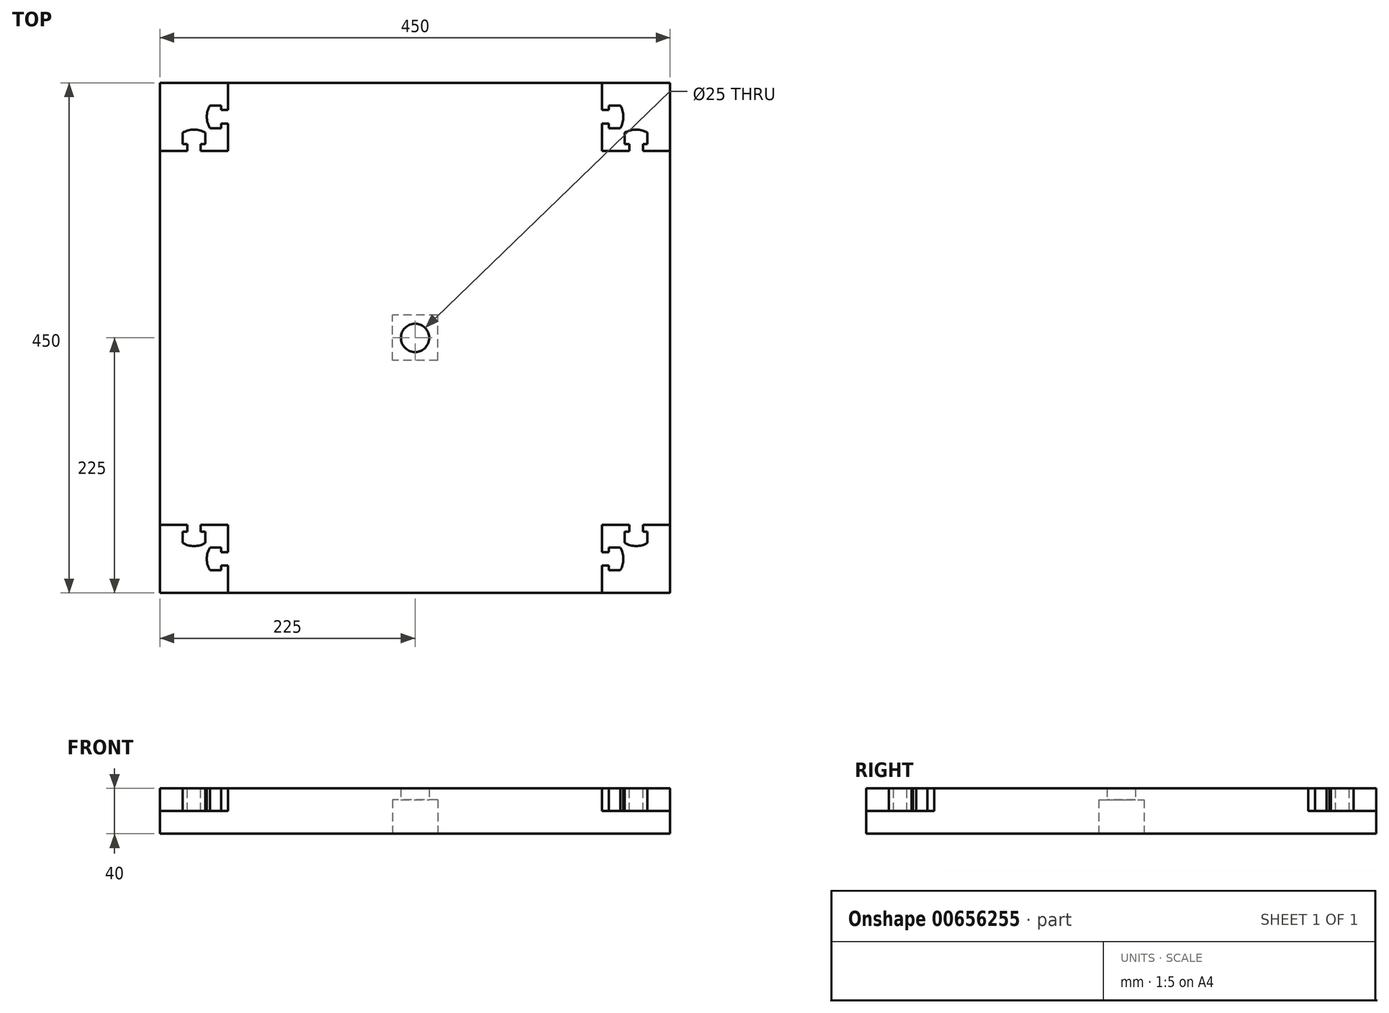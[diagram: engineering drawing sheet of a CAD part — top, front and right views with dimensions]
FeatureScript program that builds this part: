
annotation { "Feature Type Name" : "Feature", "Feature Type Description" : "" }
export const myFeature = defineFeature(function(context is Context, id is Id, definition is map)
    precondition{}
    {
        {
            var Q0;
            Q0=qCreatedBy(makeId("Top.planeOp"),FACE);
            var sketch = newSketch(context, id + "F0", { "sketchPlane" : qUnion([Q0])});
            skLineSegment(sketch, "E0.bottom", {"start": v(225, 225) * mm, "end": v(-225, 225) * mm});
            skLineSegment(sketch, "E0.top", {"start": v(225, -225) * mm, "end": v(-225, -225) * mm});
            skLineSegment(sketch, "E0.left", {"start": v(225, 225) * mm, "end": v(225, -225) * mm});
            skLineSegment(sketch, "E0.right", {"start": v(-225, 225) * mm, "end": v(-225, -225) * mm});
            skPoint(sketch, "E0.middle", {"position": v(0, 0) * mm});
            skLineSegment(sketch, "E1", {"start": v(-225, 165) * mm, "end": v(-165, 165) * mm});
            skLineSegment(sketch, "E2", {"start": v(-165, 165) * mm, "end": v(-165, 225) * mm});
            skLineSegment(sketch, "E3.MirrorCS", {"start": v(-225, -165) * mm, "end": v(-165, -165) * mm});
            skLineSegment(sketch, "E4.MirrorCS", {"start": v(-165, -165) * mm, "end": v(-165, -225) * mm});
            skLineSegment(sketch, "E5.MirrorCS", {"start": v(165, 165) * mm, "end": v(165, 225) * mm});
            skLineSegment(sketch, "E6.MirrorCS", {"start": v(225, 165) * mm, "end": v(165, 165) * mm});
            skLineSegment(sketch, "E7.MirrorCS", {"start": v(225, -165) * mm, "end": v(165, -165) * mm});
            skLineSegment(sketch, "E8.MirrorCS", {"start": v(165, -165) * mm, "end": v(165, -225) * mm});
            skSolve(sketch);
        }
        {
            var Q0;
            {var subQ4=sQuery(id+"F0.wireOp",EDGE,"E1");Q0=makeQuery(id+"F0.imprint","IMPRINT",FACE,{"disambiguationData":[TD([[makeQuery(id+"F0.imprint","IMPRINT",EDGE,{"derivedFrom":subQ4}),-1.0]])]});}
            extrude(context, id + "F1", {"entities" : qUnion([Q0]), "depth" : 40 * mm, "offsetDistance" : 25 * mm});
        }
        {
            var Q0;
            Q0=makeQuery(id+"FjshT1yFeJQ6c4P_1.boolean.opBoolean","MERGE",FACE,{"derivedFrom":[makeQuery(id+"F1.opExtrude","CAP_FACE",FACE,{"disambiguationData":[OSD([sQuery(id+"F0.wireOp",EDGE,"E0.bottom"),sQuery(id+"F0.wireOp",EDGE,"E0.top"),sQuery(id+"F0.wireOp",EDGE,"E0.left"),sQuery(id+"F0.wireOp",EDGE,"E0.right"),sQuery(id+"F0.wireOp",EDGE,"E1"),sQuery(id+"F0.wireOp",EDGE,"E2"),sQuery(id+"F0.wireOp",EDGE,"E3.MirrorCS"),sQuery(id+"F0.wireOp",EDGE,"E4.MirrorCS"),sQuery(id+"F0.wireOp",EDGE,"E5.MirrorCS"),sQuery(id+"F0.wireOp",EDGE,"E6.MirrorCS"),sQuery(id+"F0.wireOp",EDGE,"E7.MirrorCS"),sQuery(id+"F0.wireOp",EDGE,"E8.MirrorCS")])],"isStart":false}),makeQuery(id+"FjshT1yFeJQ6c4P_1.opExtrude","CAP_FACE",FACE,{"disambiguationData":[OSD([sQuery(id+"FFJnwm880kq7QGe_1.wireOp",EDGE,"IpZQhXBL-CYih-avNn-Q1HJ-p8kexNwLDa1K"),sQuery(id+"FFJnwm880kq7QGe_1.wireOp",EDGE,"DlTROYIy-GDss-TSJb-fTrS-hMDKvWpxQDZU"),sQuery(id+"FFJnwm880kq7QGe_1.wireOp",EDGE,"bTENbA7q-pvXI-0GNu-Zogf-TinsMhO668xT"),sQuery(id+"FFJnwm880kq7QGe_1.wireOp",EDGE,"CV59ftxt-n5LR-UtjV-LxEI-1yjvkEDBIUn7"),sQuery(id+"FFJnwm880kq7QGe_1.wireOp",EDGE,"VoNmPI9z-NIw1-XeOp-dFSM-tXPidPHyete0"),sQuery(id+"FFJnwm880kq7QGe_1.wireOp",EDGE,"zehCizCF-2Cgd-Ufk7-S7Fe-3zTjVviyliAL"),sQuery(id+"FFJnwm880kq7QGe_1.wireOp",EDGE,"YVxsESHW-nWeJ-Wa03-N7XI-iGOGesEvdSq9"),sQuery(id+"FFJnwm880kq7QGe_1.wireOp",EDGE,"igbJnYST-q3vv-sdNJ-N0c4-YNNVs6zLT43V")])],"isStart":true}),makeQuery(id+"FjshT1yFeJQ6c4P_1.opExtrude","CAP_FACE",FACE,{"disambiguationData":[OSD([sQuery(id+"FFJnwm880kq7QGe_1.wireOp",EDGE,"N9AVfqYu-QtxK-6Ad7-DoZk-YeEwseCOC2Zx"),sQuery(id+"FFJnwm880kq7QGe_1.wireOp",EDGE,"2Zl7s7qh-2swf-lT0q-C8q8-jJXlbCIyUqga"),sQuery(id+"FFJnwm880kq7QGe_1.wireOp",EDGE,"SRCtbRJ9-xsi2-BQLM-Kzfs-NWcCmin3xKqc"),sQuery(id+"FFJnwm880kq7QGe_1.wireOp",EDGE,"xzpgzOg8-CJKq-86Ur-ihYN-3kbHdTykDBMx"),sQuery(id+"FFJnwm880kq7QGe_1.wireOp",EDGE,"zk2CsXnC-Ixh2-XMb2-uvDl-uLO2pCno7BXc"),sQuery(id+"FFJnwm880kq7QGe_1.wireOp",EDGE,"CIBMmwUG-xv2f-loSl-yw3Y-bWYX4MdVKxOO"),sQuery(id+"FFJnwm880kq7QGe_1.wireOp",EDGE,"J3gLb0Dn-fx33-QdcY-Dk9k-6gqs1iTMeHvz"),sQuery(id+"FFJnwm880kq7QGe_1.wireOp",EDGE,"XjeUeEMd-u2qN-USpv-2rTC-nAQxEtihIGgS")])],"isStart":true}),makeQuery(id+"FjshT1yFeJQ6c4P_1.opExtrude","CAP_FACE",FACE,{"disambiguationData":[OSD([sQuery(id+"FFJnwm880kq7QGe_1.wireOp",EDGE,"395ac73a-eb74-4218-a785-b9fae4ec757f.1.0"),sQuery(id+"FFJnwm880kq7QGe_1.wireOp",EDGE,"395ac73a-eb74-4218-a785-b9fae4ec757f.1.1"),sQuery(id+"FFJnwm880kq7QGe_1.wireOp",EDGE,"395ac73a-eb74-4218-a785-b9fae4ec757f.1.2"),sQuery(id+"FFJnwm880kq7QGe_1.wireOp",EDGE,"395ac73a-eb74-4218-a785-b9fae4ec757f.1.3"),sQuery(id+"FFJnwm880kq7QGe_1.wireOp",EDGE,"395ac73a-eb74-4218-a785-b9fae4ec757f.1.4"),sQuery(id+"FFJnwm880kq7QGe_1.wireOp",EDGE,"395ac73a-eb74-4218-a785-b9fae4ec757f.1.5"),sQuery(id+"FFJnwm880kq7QGe_1.wireOp",EDGE,"395ac73a-eb74-4218-a785-b9fae4ec757f.1.6"),sQuery(id+"FFJnwm880kq7QGe_1.wireOp",EDGE,"395ac73a-eb74-4218-a785-b9fae4ec757f.1.7")])],"isStart":true}),makeQuery(id+"FjshT1yFeJQ6c4P_1.opExtrude","CAP_FACE",FACE,{"disambiguationData":[OSD([sQuery(id+"FFJnwm880kq7QGe_1.wireOp",EDGE,"395ac73a-eb74-4218-a785-b9fae4ec757f.1.8"),sQuery(id+"FFJnwm880kq7QGe_1.wireOp",EDGE,"395ac73a-eb74-4218-a785-b9fae4ec757f.1.9"),sQuery(id+"FFJnwm880kq7QGe_1.wireOp",EDGE,"395ac73a-eb74-4218-a785-b9fae4ec757f.1.10"),sQuery(id+"FFJnwm880kq7QGe_1.wireOp",EDGE,"395ac73a-eb74-4218-a785-b9fae4ec757f.1.11"),sQuery(id+"FFJnwm880kq7QGe_1.wireOp",EDGE,"395ac73a-eb74-4218-a785-b9fae4ec757f.1.12"),sQuery(id+"FFJnwm880kq7QGe_1.wireOp",EDGE,"395ac73a-eb74-4218-a785-b9fae4ec757f.1.13"),sQuery(id+"FFJnwm880kq7QGe_1.wireOp",EDGE,"395ac73a-eb74-4218-a785-b9fae4ec757f.1.14"),sQuery(id+"FFJnwm880kq7QGe_1.wireOp",EDGE,"395ac73a-eb74-4218-a785-b9fae4ec757f.1.15")])],"isStart":true}),makeQuery(id+"FjshT1yFeJQ6c4P_1.opExtrude","CAP_FACE",FACE,{"disambiguationData":[OSD([sQuery(id+"FFJnwm880kq7QGe_1.wireOp",EDGE,"395ac73a-eb74-4218-a785-b9fae4ec757f.2.0"),sQuery(id+"FFJnwm880kq7QGe_1.wireOp",EDGE,"395ac73a-eb74-4218-a785-b9fae4ec757f.2.1"),sQuery(id+"FFJnwm880kq7QGe_1.wireOp",EDGE,"395ac73a-eb74-4218-a785-b9fae4ec757f.2.2"),sQuery(id+"FFJnwm880kq7QGe_1.wireOp",EDGE,"395ac73a-eb74-4218-a785-b9fae4ec757f.2.3"),sQuery(id+"FFJnwm880kq7QGe_1.wireOp",EDGE,"395ac73a-eb74-4218-a785-b9fae4ec757f.2.4"),sQuery(id+"FFJnwm880kq7QGe_1.wireOp",EDGE,"395ac73a-eb74-4218-a785-b9fae4ec757f.2.5"),sQuery(id+"FFJnwm880kq7QGe_1.wireOp",EDGE,"395ac73a-eb74-4218-a785-b9fae4ec757f.2.6"),sQuery(id+"FFJnwm880kq7QGe_1.wireOp",EDGE,"395ac73a-eb74-4218-a785-b9fae4ec757f.2.7")])],"isStart":true}),makeQuery(id+"FjshT1yFeJQ6c4P_1.opExtrude","CAP_FACE",FACE,{"disambiguationData":[OSD([sQuery(id+"FFJnwm880kq7QGe_1.wireOp",EDGE,"395ac73a-eb74-4218-a785-b9fae4ec757f.2.8"),sQuery(id+"FFJnwm880kq7QGe_1.wireOp",EDGE,"395ac73a-eb74-4218-a785-b9fae4ec757f.2.9"),sQuery(id+"FFJnwm880kq7QGe_1.wireOp",EDGE,"395ac73a-eb74-4218-a785-b9fae4ec757f.2.10"),sQuery(id+"FFJnwm880kq7QGe_1.wireOp",EDGE,"395ac73a-eb74-4218-a785-b9fae4ec757f.2.11"),sQuery(id+"FFJnwm880kq7QGe_1.wireOp",EDGE,"395ac73a-eb74-4218-a785-b9fae4ec757f.2.12"),sQuery(id+"FFJnwm880kq7QGe_1.wireOp",EDGE,"395ac73a-eb74-4218-a785-b9fae4ec757f.2.13"),sQuery(id+"FFJnwm880kq7QGe_1.wireOp",EDGE,"395ac73a-eb74-4218-a785-b9fae4ec757f.2.14"),sQuery(id+"FFJnwm880kq7QGe_1.wireOp",EDGE,"395ac73a-eb74-4218-a785-b9fae4ec757f.2.15")])],"isStart":true}),makeQuery(id+"FjshT1yFeJQ6c4P_1.opExtrude","CAP_FACE",FACE,{"disambiguationData":[OSD([sQuery(id+"FFJnwm880kq7QGe_1.wireOp",EDGE,"395ac73a-eb74-4218-a785-b9fae4ec757f.3.0"),sQuery(id+"FFJnwm880kq7QGe_1.wireOp",EDGE,"395ac73a-eb74-4218-a785-b9fae4ec757f.3.1"),sQuery(id+"FFJnwm880kq7QGe_1.wireOp",EDGE,"395ac73a-eb74-4218-a785-b9fae4ec757f.3.2"),sQuery(id+"FFJnwm880kq7QGe_1.wireOp",EDGE,"395ac73a-eb74-4218-a785-b9fae4ec757f.3.3"),sQuery(id+"FFJnwm880kq7QGe_1.wireOp",EDGE,"395ac73a-eb74-4218-a785-b9fae4ec757f.3.4"),sQuery(id+"FFJnwm880kq7QGe_1.wireOp",EDGE,"395ac73a-eb74-4218-a785-b9fae4ec757f.3.5"),sQuery(id+"FFJnwm880kq7QGe_1.wireOp",EDGE,"395ac73a-eb74-4218-a785-b9fae4ec757f.3.6"),sQuery(id+"FFJnwm880kq7QGe_1.wireOp",EDGE,"395ac73a-eb74-4218-a785-b9fae4ec757f.3.7")])],"isStart":true}),makeQuery(id+"FjshT1yFeJQ6c4P_1.opExtrude","CAP_FACE",FACE,{"disambiguationData":[OSD([sQuery(id+"FFJnwm880kq7QGe_1.wireOp",EDGE,"395ac73a-eb74-4218-a785-b9fae4ec757f.3.8"),sQuery(id+"FFJnwm880kq7QGe_1.wireOp",EDGE,"395ac73a-eb74-4218-a785-b9fae4ec757f.3.9"),sQuery(id+"FFJnwm880kq7QGe_1.wireOp",EDGE,"395ac73a-eb74-4218-a785-b9fae4ec757f.3.10"),sQuery(id+"FFJnwm880kq7QGe_1.wireOp",EDGE,"395ac73a-eb74-4218-a785-b9fae4ec757f.3.11"),sQuery(id+"FFJnwm880kq7QGe_1.wireOp",EDGE,"395ac73a-eb74-4218-a785-b9fae4ec757f.3.12"),sQuery(id+"FFJnwm880kq7QGe_1.wireOp",EDGE,"395ac73a-eb74-4218-a785-b9fae4ec757f.3.13"),sQuery(id+"FFJnwm880kq7QGe_1.wireOp",EDGE,"395ac73a-eb74-4218-a785-b9fae4ec757f.3.14"),sQuery(id+"FFJnwm880kq7QGe_1.wireOp",EDGE,"395ac73a-eb74-4218-a785-b9fae4ec757f.3.15")])],"isStart":true})]});
            var sketch = newSketch(context, id + "F2", { "sketchPlane" : qUnion([Q0])});
            skSolve(sketch);
        }
        {
            var Q0;
            Q0 = qSketchRegion(id + "F0", true);
            extrude(context, id + "F3", {"entities" : qUnion([Q0]), "operationType" : NewBodyOperationType.ADD, "depth" : 20 * mm, "offsetDistance" : 25 * mm});
        }
        {
            var Q0;
            Q0=makeQuery(id+"F2.imprint","IMPRINT",FACE,{"disambiguationData":[TD([[makeQuery(id+"F2.imprint","IMPRINT",EDGE,{"derivedFrom":makeQuery(id+"F1.opExtrude","CAP_EDGE",EDGE,{"disambiguationData":[OSD([sQuery(id+"F0.wireOp",EDGE,"E0.bottom")])],"isStart":false})}),1.0]])]});
            var sketch = newSketch(context, id + "F4", { "sketchPlane" : qUnion([Q0])});
            skLineSegment(sketch, "E9", {"start": v(-201, 165) * mm, "end": v(-201, 171) * mm});
            skLineSegment(sketch, "E10", {"start": v(-201, 171) * mm, "end": v(-205, 171) * mm});
            skLineSegment(sketch, "E11", {"start": v(-205, 171) * mm, "end": v(-205, 181) * mm});
            skLineSegment(sketch, "E12", {"start": v(-189, 165) * mm, "end": v(-189, 171) * mm});
            skLineSegment(sketch, "E13", {"start": v(-189, 171) * mm, "end": v(-185, 171) * mm});
            skLineSegment(sketch, "E14", {"start": v(-185, 171) * mm, "end": v(-185, 181) * mm});
            skLineSegment(sketch, "E15", {"start": v(-165, 189) * mm, "end": v(-171, 189) * mm});
            skLineSegment(sketch, "E16", {"start": v(-201, 165) * mm, "end": v(-189, 165) * mm});
            skArc(sketch, "E17", {"start": v(-185, 181) * mm, "mid": v(-195, 183.68) * mm, "end": v(-205, 181) * mm});
            skLineSegment(sketch, "E18", {"start": v(-165, 201) * mm, "end": v(-171, 201) * mm});
            skLineSegment(sketch, "E19", {"start": v(-171, 201) * mm, "end": v(-171, 205) * mm});
            skLineSegment(sketch, "E20", {"start": v(-171, 205) * mm, "end": v(-181, 205) * mm});
            skLineSegment(sketch, "E21", {"start": v(-171, 189) * mm, "end": v(-171, 185) * mm});
            skLineSegment(sketch, "E22", {"start": v(-171, 185) * mm, "end": v(-181, 185) * mm});
            skLineSegment(sketch, "E23", {"start": v(-165, 201) * mm, "end": v(-165, 189) * mm});
            skArc(sketch, "E24", {"start": v(-181, 205) * mm, "mid": v(-183.68, 195) * mm, "end": v(-181, 185) * mm});
            skLineSegment(sketch, "E25.1.0", {"start": v(-185, -171) * mm, "end": v(-185, -181) * mm});
            skArc(sketch, "E25.1.1", {"start": v(-205, -181) * mm, "mid": v(-195, -183.68) * mm, "end": v(-185, -181) * mm});
            skLineSegment(sketch, "E25.1.2", {"start": v(-171, -205) * mm, "end": v(-181, -205) * mm});
            skLineSegment(sketch, "E25.1.3", {"start": v(-171, -185) * mm, "end": v(-181, -185) * mm});
            skArc(sketch, "E25.1.4", {"start": v(-181, -185) * mm, "mid": v(-183.68, -195) * mm, "end": v(-181, -205) * mm});
            skLineSegment(sketch, "E25.1.5", {"start": v(-205, -171) * mm, "end": v(-205, -181) * mm});
            skLineSegment(sketch, "E25.1.6", {"start": v(-201, -165) * mm, "end": v(-189, -165) * mm});
            skLineSegment(sketch, "E25.1.7", {"start": v(-165, -201) * mm, "end": v(-165, -189) * mm});
            skLineSegment(sketch, "E25.1.8", {"start": v(-165, -201) * mm, "end": v(-171, -201) * mm});
            skLineSegment(sketch, "E25.1.9", {"start": v(-171, -201) * mm, "end": v(-171, -205) * mm});
            skLineSegment(sketch, "E25.1.10", {"start": v(-165, -189) * mm, "end": v(-171, -189) * mm});
            skLineSegment(sketch, "E25.1.11", {"start": v(-171, -189) * mm, "end": v(-171, -185) * mm});
            skLineSegment(sketch, "E25.1.12", {"start": v(-189, -165) * mm, "end": v(-189, -171) * mm});
            skLineSegment(sketch, "E25.1.13", {"start": v(-201, -165) * mm, "end": v(-201, -171) * mm});
            skLineSegment(sketch, "E25.1.14", {"start": v(-201, -171) * mm, "end": v(-205, -171) * mm});
            skLineSegment(sketch, "E25.1.15", {"start": v(-189, -171) * mm, "end": v(-185, -171) * mm});
            skLineSegment(sketch, "E25.2.0", {"start": v(171, -185) * mm, "end": v(181, -185) * mm});
            skArc(sketch, "E25.2.1", {"start": v(181, -205) * mm, "mid": v(183.68, -195) * mm, "end": v(181, -185) * mm});
            skLineSegment(sketch, "E25.2.2", {"start": v(205, -171) * mm, "end": v(205, -181) * mm});
            skLineSegment(sketch, "E25.2.3", {"start": v(185, -171) * mm, "end": v(185, -181) * mm});
            skArc(sketch, "E25.2.4", {"start": v(185, -181) * mm, "mid": v(195, -183.68) * mm, "end": v(205, -181) * mm});
            skLineSegment(sketch, "E25.2.5", {"start": v(171, -205) * mm, "end": v(181, -205) * mm});
            skLineSegment(sketch, "E25.2.6", {"start": v(165, -201) * mm, "end": v(165, -189) * mm});
            skLineSegment(sketch, "E25.2.7", {"start": v(201, -165) * mm, "end": v(189, -165) * mm});
            skLineSegment(sketch, "E25.2.8", {"start": v(201, -165) * mm, "end": v(201, -171) * mm});
            skLineSegment(sketch, "E25.2.9", {"start": v(201, -171) * mm, "end": v(205, -171) * mm});
            skLineSegment(sketch, "E25.2.10", {"start": v(189, -165) * mm, "end": v(189, -171) * mm});
            skLineSegment(sketch, "E25.2.11", {"start": v(189, -171) * mm, "end": v(185, -171) * mm});
            skLineSegment(sketch, "E25.2.12", {"start": v(165, -189) * mm, "end": v(171, -189) * mm});
            skLineSegment(sketch, "E25.2.13", {"start": v(165, -201) * mm, "end": v(171, -201) * mm});
            skLineSegment(sketch, "E25.2.14", {"start": v(171, -201) * mm, "end": v(171, -205) * mm});
            skLineSegment(sketch, "E25.2.15", {"start": v(171, -189) * mm, "end": v(171, -185) * mm});
            skLineSegment(sketch, "E25.3.0", {"start": v(185, 171) * mm, "end": v(185, 181) * mm});
            skArc(sketch, "E25.3.1", {"start": v(205, 181) * mm, "mid": v(195, 183.68) * mm, "end": v(185, 181) * mm});
            skLineSegment(sketch, "E25.3.2", {"start": v(171, 205) * mm, "end": v(181, 205) * mm});
            skLineSegment(sketch, "E25.3.3", {"start": v(171, 185) * mm, "end": v(181, 185) * mm});
            skArc(sketch, "E25.3.4", {"start": v(181, 185) * mm, "mid": v(183.68, 195) * mm, "end": v(181, 205) * mm});
            skLineSegment(sketch, "E25.3.5", {"start": v(205, 171) * mm, "end": v(205, 181) * mm});
            skLineSegment(sketch, "E25.3.6", {"start": v(201, 165) * mm, "end": v(189, 165) * mm});
            skLineSegment(sketch, "E25.3.7", {"start": v(165, 201) * mm, "end": v(165, 189) * mm});
            skLineSegment(sketch, "E25.3.8", {"start": v(165, 201) * mm, "end": v(171, 201) * mm});
            skLineSegment(sketch, "E25.3.9", {"start": v(171, 201) * mm, "end": v(171, 205) * mm});
            skLineSegment(sketch, "E25.3.10", {"start": v(165, 189) * mm, "end": v(171, 189) * mm});
            skLineSegment(sketch, "E25.3.11", {"start": v(171, 189) * mm, "end": v(171, 185) * mm});
            skLineSegment(sketch, "E25.3.12", {"start": v(189, 165) * mm, "end": v(189, 171) * mm});
            skLineSegment(sketch, "E25.3.13", {"start": v(201, 165) * mm, "end": v(201, 171) * mm});
            skLineSegment(sketch, "E25.3.14", {"start": v(201, 171) * mm, "end": v(205, 171) * mm});
            skLineSegment(sketch, "E25.3.15", {"start": v(189, 171) * mm, "end": v(185, 171) * mm});
            skPoint(sketch, "E25.center", {"position": v(0, 0) * mm});
            skSolve(sketch);
        }
        {
            var Q0;
            Q0=makeQuery(id+"F4.imprint","IMPRINT",FACE,{"disambiguationData":[TD([[makeQuery(id+"F4.imprint","IMPRINT",EDGE,{"derivedFrom":sQuery(id+"F4.wireOp",EDGE,"E9")}),-1.0]])]});
            var Q1;
            Q1=makeQuery(id+"F4.imprint","IMPRINT",FACE,{"disambiguationData":[TD([[makeQuery(id+"F4.imprint","IMPRINT",EDGE,{"derivedFrom":sQuery(id+"F4.wireOp",EDGE,"E15")}),-1.0]])]});
            var Q2;
            Q2=makeQuery(id+"F4.imprint","IMPRINT",FACE,{"disambiguationData":[TD([[makeQuery(id+"F4.imprint","IMPRINT",EDGE,{"derivedFrom":sQuery(id+"F4.wireOp",EDGE,"E25.3.2")}),-1.0]])]});
            var Q3;
            Q3=makeQuery(id+"F4.imprint","IMPRINT",FACE,{"disambiguationData":[TD([[makeQuery(id+"F4.imprint","IMPRINT",EDGE,{"derivedFrom":sQuery(id+"F4.wireOp",EDGE,"E25.3.0")}),-1.0]])]});
            var Q4;
            Q4=makeQuery(id+"F4.imprint","IMPRINT",FACE,{"disambiguationData":[TD([[makeQuery(id+"F4.imprint","IMPRINT",EDGE,{"derivedFrom":sQuery(id+"F4.wireOp",EDGE,"E25.1.2")}),-1.0]])]});
            var Q5;
            Q5=makeQuery(id+"F4.imprint","IMPRINT",FACE,{"disambiguationData":[TD([[makeQuery(id+"F4.imprint","IMPRINT",EDGE,{"derivedFrom":sQuery(id+"F4.wireOp",EDGE,"E25.1.0")}),-1.0]])]});
            var Q6;
            Q6=makeQuery(id+"F4.imprint","IMPRINT",FACE,{"disambiguationData":[TD([[makeQuery(id+"F4.imprint","IMPRINT",EDGE,{"derivedFrom":sQuery(id+"F4.wireOp",EDGE,"E25.2.2")}),-1.0]])]});
            var Q7;
            Q7=makeQuery(id+"F4.imprint","IMPRINT",FACE,{"disambiguationData":[TD([[makeQuery(id+"F4.imprint","IMPRINT",EDGE,{"derivedFrom":sQuery(id+"F4.wireOp",EDGE,"E25.2.0")}),-1.0]])]});
            var Q8;
            {var subQ0=sQuery(id+"F0.wireOp",EDGE,"E0.right");var subQ1=sQuery(id+"F0.wireOp",EDGE,"E0.top");Q8=makeQuery(id+"F3.boolean.opBoolean","SPLIT",FACE,{"disambiguationData":[TD([makeQuery(id+"F1.opExtrude","SWEPT_FACE",FACE,{"disambiguationData":[OSD([sQuery(id+"F0.wireOp",EDGE,"E3.MirrorCS")])]})])],"derivedFrom":makeQuery(id+"F3.opExtrude","CAP_FACE",FACE,{"disambiguationData":[OSD([sQuery(id+"F0.wireOp",EDGE,"E0.bottom"),subQ1,sQuery(id+"F0.wireOp",EDGE,"E0.left"),subQ0])],"isStart":false})});}
            extrude(context, id + "F5", {"entities" : qUnion([Q0, Q1, Q2, Q3, Q4, Q5, Q6, Q7]), "operationType" : NewBodyOperationType.ADD, "endBound" : BoundingType.UP_TO_SURFACE, "oppositeDirection" : true, "depth" : 25 * mm, "endBoundEntityFace" : qUnion([Q8]), "offsetDistance" : 25 * mm});
        }
        {
            var Q0;
            {var subQ0=sQuery(id+"F0.wireOp",EDGE,"E0.right");var subQ1=sQuery(id+"F0.wireOp",EDGE,"E0.left");var subQ2=sQuery(id+"F0.wireOp",EDGE,"E0.top");var subQ3=sQuery(id+"F0.wireOp",EDGE,"E0.bottom");Q0=makeQuery(id+"F3.boolean.opBoolean","MERGE",FACE,{"derivedFrom":[makeQuery(id+"F1.opExtrude","CAP_FACE",FACE,{"disambiguationData":[OSD([subQ3,subQ2,subQ1,subQ0,sQuery(id+"F0.wireOp",EDGE,"E1"),sQuery(id+"F0.wireOp",EDGE,"E2"),sQuery(id+"F0.wireOp",EDGE,"E3.MirrorCS"),sQuery(id+"F0.wireOp",EDGE,"E4.MirrorCS"),sQuery(id+"F0.wireOp",EDGE,"E5.MirrorCS"),sQuery(id+"F0.wireOp",EDGE,"E6.MirrorCS"),sQuery(id+"F0.wireOp",EDGE,"E7.MirrorCS"),sQuery(id+"F0.wireOp",EDGE,"E8.MirrorCS")])],"isStart":true}),makeQuery(id+"F3.opExtrude","CAP_FACE",FACE,{"disambiguationData":[OSD([subQ3,subQ2,subQ1,subQ0])],"isStart":true})]});}
            var sketch = newSketch(context, id + "F6", { "sketchPlane" : qUnion([Q0])});
            skLineSegment(sketch, "E26.bottom", {"start": v(20, 20) * mm, "end": v(-20, 20) * mm});
            skLineSegment(sketch, "E26.top", {"start": v(20, -20) * mm, "end": v(-20, -20) * mm});
            skLineSegment(sketch, "E26.left", {"start": v(20, 20) * mm, "end": v(20, -20) * mm});
            skLineSegment(sketch, "E26.right", {"start": v(-20, 20) * mm, "end": v(-20, -20) * mm});
            skPoint(sketch, "E26.middle", {"position": v(0, 0) * mm});
            skCircle(sketch, "E27", {"center": v(0, 0) * mm, "radius": 12.5 * mm});
            skSolve(sketch);
        }
        {
            var Q0;
            Q0=makeQuery(id+"F6.imprint","IMPRINT",FACE,{"disambiguationData":[TD([[makeQuery(id+"F6.imprint","IMPRINT",EDGE,{"derivedFrom":sQuery(id+"F6.wireOp",EDGE,"E26.bottom")}),1.0]])]});
            extrude(context, id + "F7", {"entities" : qUnion([Q0]), "operationType" : NewBodyOperationType.REMOVE, "oppositeDirection" : true, "depth" : 30 * mm, "offsetDistance" : 25 * mm});
        }
        {
            var Q0;
            {var subQ0=sQuery(id+"F0.wireOp",EDGE,"E0.right");var subQ1=sQuery(id+"F0.wireOp",EDGE,"E0.left");var subQ2=sQuery(id+"F0.wireOp",EDGE,"E0.top");var subQ3=sQuery(id+"F0.wireOp",EDGE,"E0.bottom");Q0=makeQuery(id+"F7.boolean.opBoolean","SPLIT",FACE,{"disambiguationData":[TD([makeQuery(id+"F7.opExtrude","SWEPT_FACE",FACE,{"disambiguationData":[OSD([sQuery(id+"F6.wireOp",EDGE,"E27")])]})])],"derivedFrom":makeQuery(id+"F3.boolean.opBoolean","MERGE",FACE,{"derivedFrom":[makeQuery(id+"F1.opExtrude","CAP_FACE",FACE,{"disambiguationData":[OSD([subQ3,subQ2,subQ1,subQ0,sQuery(id+"F0.wireOp",EDGE,"E1"),sQuery(id+"F0.wireOp",EDGE,"E2"),sQuery(id+"F0.wireOp",EDGE,"E3.MirrorCS"),sQuery(id+"F0.wireOp",EDGE,"E4.MirrorCS"),sQuery(id+"F0.wireOp",EDGE,"E5.MirrorCS"),sQuery(id+"F0.wireOp",EDGE,"E6.MirrorCS"),sQuery(id+"F0.wireOp",EDGE,"E7.MirrorCS"),sQuery(id+"F0.wireOp",EDGE,"E8.MirrorCS")])],"isStart":true}),makeQuery(id+"F3.opExtrude","CAP_FACE",FACE,{"disambiguationData":[OSD([subQ3,subQ2,subQ1,subQ0])],"isStart":true})]})});}
            var Q1;
            Q1=makeQuery(id+"F5.boolean.opBoolean","MERGE",FACE,{"derivedFrom":[makeQuery(id+"F1.opExtrude","CAP_FACE",FACE,{"disambiguationData":[OSD([sQuery(id+"F0.wireOp",EDGE,"E0.bottom"),sQuery(id+"F0.wireOp",EDGE,"E0.top"),sQuery(id+"F0.wireOp",EDGE,"E0.left"),sQuery(id+"F0.wireOp",EDGE,"E0.right"),sQuery(id+"F0.wireOp",EDGE,"E1"),sQuery(id+"F0.wireOp",EDGE,"E2"),sQuery(id+"F0.wireOp",EDGE,"E3.MirrorCS"),sQuery(id+"F0.wireOp",EDGE,"E4.MirrorCS"),sQuery(id+"F0.wireOp",EDGE,"E5.MirrorCS"),sQuery(id+"F0.wireOp",EDGE,"E6.MirrorCS"),sQuery(id+"F0.wireOp",EDGE,"E7.MirrorCS"),sQuery(id+"F0.wireOp",EDGE,"E8.MirrorCS")])],"isStart":false}),makeQuery(id+"F5.opExtrude","CAP_FACE",FACE,{"disambiguationData":[OSD([sQuery(id+"F4.wireOp",EDGE,"E9"),sQuery(id+"F4.wireOp",EDGE,"E10"),sQuery(id+"F4.wireOp",EDGE,"E11"),sQuery(id+"F4.wireOp",EDGE,"E12"),sQuery(id+"F4.wireOp",EDGE,"E13"),sQuery(id+"F4.wireOp",EDGE,"E14"),sQuery(id+"F4.wireOp",EDGE,"E16"),sQuery(id+"F4.wireOp",EDGE,"E17")])],"isStart":true}),makeQuery(id+"F5.opExtrude","CAP_FACE",FACE,{"disambiguationData":[OSD([sQuery(id+"F4.wireOp",EDGE,"E15"),sQuery(id+"F4.wireOp",EDGE,"E18"),sQuery(id+"F4.wireOp",EDGE,"E19"),sQuery(id+"F4.wireOp",EDGE,"E20"),sQuery(id+"F4.wireOp",EDGE,"E21"),sQuery(id+"F4.wireOp",EDGE,"E22"),sQuery(id+"F4.wireOp",EDGE,"E23"),sQuery(id+"F4.wireOp",EDGE,"E24")])],"isStart":true}),makeQuery(id+"F5.opExtrude","CAP_FACE",FACE,{"disambiguationData":[OSD([sQuery(id+"F4.wireOp",EDGE,"E25.1.0"),sQuery(id+"F4.wireOp",EDGE,"E25.1.1"),sQuery(id+"F4.wireOp",EDGE,"E25.1.5"),sQuery(id+"F4.wireOp",EDGE,"E25.1.6"),sQuery(id+"F4.wireOp",EDGE,"E25.1.12"),sQuery(id+"F4.wireOp",EDGE,"E25.1.13"),sQuery(id+"F4.wireOp",EDGE,"E25.1.14"),sQuery(id+"F4.wireOp",EDGE,"E25.1.15")])],"isStart":true}),makeQuery(id+"F5.opExtrude","CAP_FACE",FACE,{"disambiguationData":[OSD([sQuery(id+"F4.wireOp",EDGE,"E25.1.2"),sQuery(id+"F4.wireOp",EDGE,"E25.1.3"),sQuery(id+"F4.wireOp",EDGE,"E25.1.4"),sQuery(id+"F4.wireOp",EDGE,"E25.1.7"),sQuery(id+"F4.wireOp",EDGE,"E25.1.8"),sQuery(id+"F4.wireOp",EDGE,"E25.1.9"),sQuery(id+"F4.wireOp",EDGE,"E25.1.10"),sQuery(id+"F4.wireOp",EDGE,"E25.1.11")])],"isStart":true}),makeQuery(id+"F5.opExtrude","CAP_FACE",FACE,{"disambiguationData":[OSD([sQuery(id+"F4.wireOp",EDGE,"E25.2.0"),sQuery(id+"F4.wireOp",EDGE,"E25.2.1"),sQuery(id+"F4.wireOp",EDGE,"E25.2.5"),sQuery(id+"F4.wireOp",EDGE,"E25.2.6"),sQuery(id+"F4.wireOp",EDGE,"E25.2.12"),sQuery(id+"F4.wireOp",EDGE,"E25.2.13"),sQuery(id+"F4.wireOp",EDGE,"E25.2.14"),sQuery(id+"F4.wireOp",EDGE,"E25.2.15")])],"isStart":true}),makeQuery(id+"F5.opExtrude","CAP_FACE",FACE,{"disambiguationData":[OSD([sQuery(id+"F4.wireOp",EDGE,"E25.2.2"),sQuery(id+"F4.wireOp",EDGE,"E25.2.3"),sQuery(id+"F4.wireOp",EDGE,"E25.2.4"),sQuery(id+"F4.wireOp",EDGE,"E25.2.7"),sQuery(id+"F4.wireOp",EDGE,"E25.2.8"),sQuery(id+"F4.wireOp",EDGE,"E25.2.9"),sQuery(id+"F4.wireOp",EDGE,"E25.2.10"),sQuery(id+"F4.wireOp",EDGE,"E25.2.11")])],"isStart":true}),makeQuery(id+"F5.opExtrude","CAP_FACE",FACE,{"disambiguationData":[OSD([sQuery(id+"F4.wireOp",EDGE,"E25.3.0"),sQuery(id+"F4.wireOp",EDGE,"E25.3.1"),sQuery(id+"F4.wireOp",EDGE,"E25.3.5"),sQuery(id+"F4.wireOp",EDGE,"E25.3.6"),sQuery(id+"F4.wireOp",EDGE,"E25.3.12"),sQuery(id+"F4.wireOp",EDGE,"E25.3.13"),sQuery(id+"F4.wireOp",EDGE,"E25.3.14"),sQuery(id+"F4.wireOp",EDGE,"E25.3.15")])],"isStart":true}),makeQuery(id+"F5.opExtrude","CAP_FACE",FACE,{"disambiguationData":[OSD([sQuery(id+"F4.wireOp",EDGE,"E25.3.2"),sQuery(id+"F4.wireOp",EDGE,"E25.3.3"),sQuery(id+"F4.wireOp",EDGE,"E25.3.4"),sQuery(id+"F4.wireOp",EDGE,"E25.3.7"),sQuery(id+"F4.wireOp",EDGE,"E25.3.8"),sQuery(id+"F4.wireOp",EDGE,"E25.3.9"),sQuery(id+"F4.wireOp",EDGE,"E25.3.10"),sQuery(id+"F4.wireOp",EDGE,"E25.3.11")])],"isStart":true})]});
            extrude(context, id + "F8", {"entities" : qUnion([Q0]), "operationType" : NewBodyOperationType.REMOVE, "endBound" : BoundingType.UP_TO_SURFACE, "oppositeDirection" : true, "depth" : 25 * mm, "endBoundEntityFace" : qUnion([Q1]), "offsetDistance" : 25 * mm});
        }
    });
